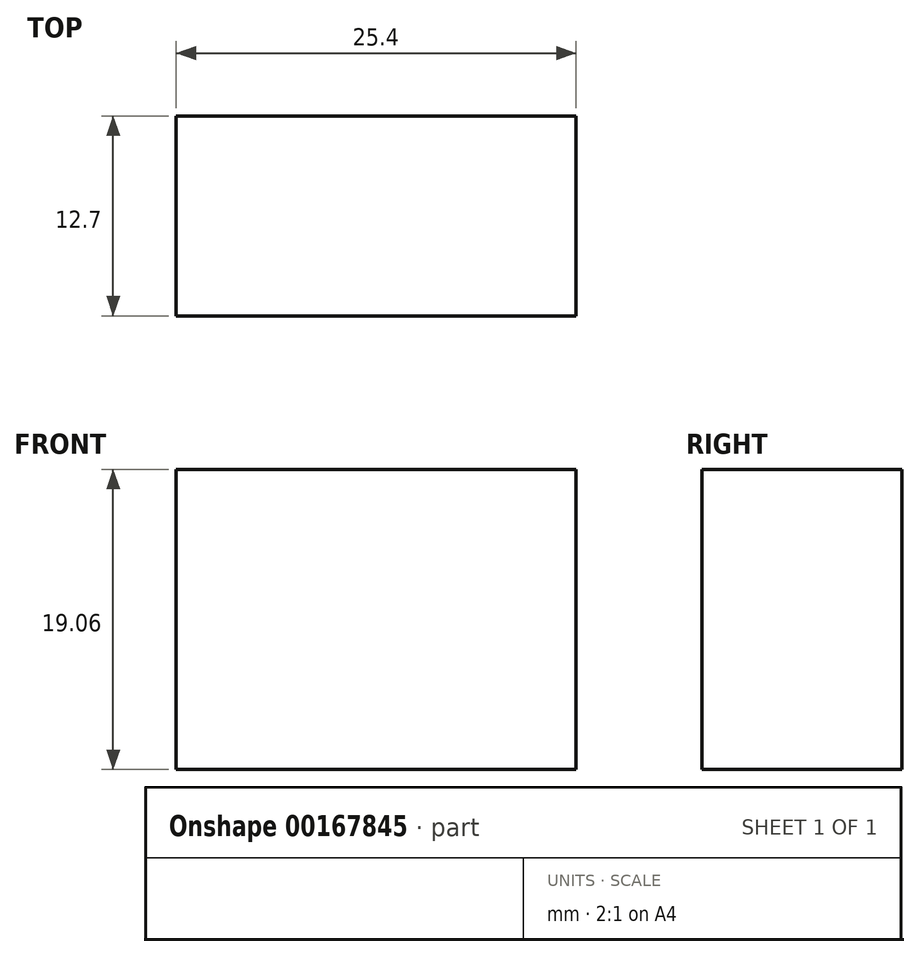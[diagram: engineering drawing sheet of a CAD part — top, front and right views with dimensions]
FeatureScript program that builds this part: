
annotation { "Feature Type Name" : "Feature", "Feature Type Description" : "" }
export const myFeature = defineFeature(function(context is Context, id is Id, definition is map)
    precondition{}
    {
        {
            var Q0;
            Q0=qCreatedBy(makeId("Front.planeOp"),FACE);
            var sketch = newSketch(context, id + "F0", { "sketchPlane" : qUnion([Q0])});
            skLineSegment(sketch, "E0.bottom", {"start": v(15.08, 9.53) * mm, "end": v(-10.32, 9.52) * mm});
            skLineSegment(sketch, "E0.top", {"start": v(15.08, -9.52) * mm, "end": v(-10.32, -9.53) * mm});
            skLineSegment(sketch, "E0.left", {"start": v(15.08, 9.53) * mm, "end": v(15.08, -9.52) * mm});
            skLineSegment(sketch, "E0.right", {"start": v(-10.32, 9.52) * mm, "end": v(-10.32, -9.53) * mm});
            skPoint(sketch, "E0.middle", {"position": v(2.38, 0) * mm});
            skSolve(sketch);
        }
        {
            var Q0;
            Q0 = qSketchRegion(id + "F0", true);
            extrude(context, id + "F1", {"entities" : qUnion([Q0]), "depth" : 12.7 * mm});
        }
    });
